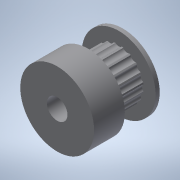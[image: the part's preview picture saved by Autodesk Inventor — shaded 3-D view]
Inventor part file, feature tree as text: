
AUTODESK INVENTOR PART (.ipt)
format: ipt  version: 2022 (Build 260153000, 153)  size: 168,960 bytes
history: native  units: mm
features: sketch x2, revolve x1, extrude x1, pattern_circular x1
ambient origin geometry x8: Origin, YZ Plane, XZ Plane, XY Plane, X Axis, Y Axis, Z Axis, Center Point
bodies: Solid1 (feature_tree)
feature tree (5):
  revolve  "Revolution1"  [1 undecoded]
  extrude  "Extrusion1"  Depth=9.0mm
  pattern_circular  "Circular Pattern1"  [2 undecoded]
  sketch  "Sketch1"  dims[d0=2.5mm d1=7.5mm]
  sketch  "Sketch2"  dims[d2=7.5mm d3=9.0mm d4=1.0mm d6=6.1mm d7=90.0deg d8=2.0mm d9=6.7mm d10=10.0mm d11=0.0mm d12=200.0mm d13=360.0deg]
note: 3 required parameter values undecoded (feature->parameter linkage not recoverable at this tier; creation-order binding heuristic only, values carry confidence <= 0.55)